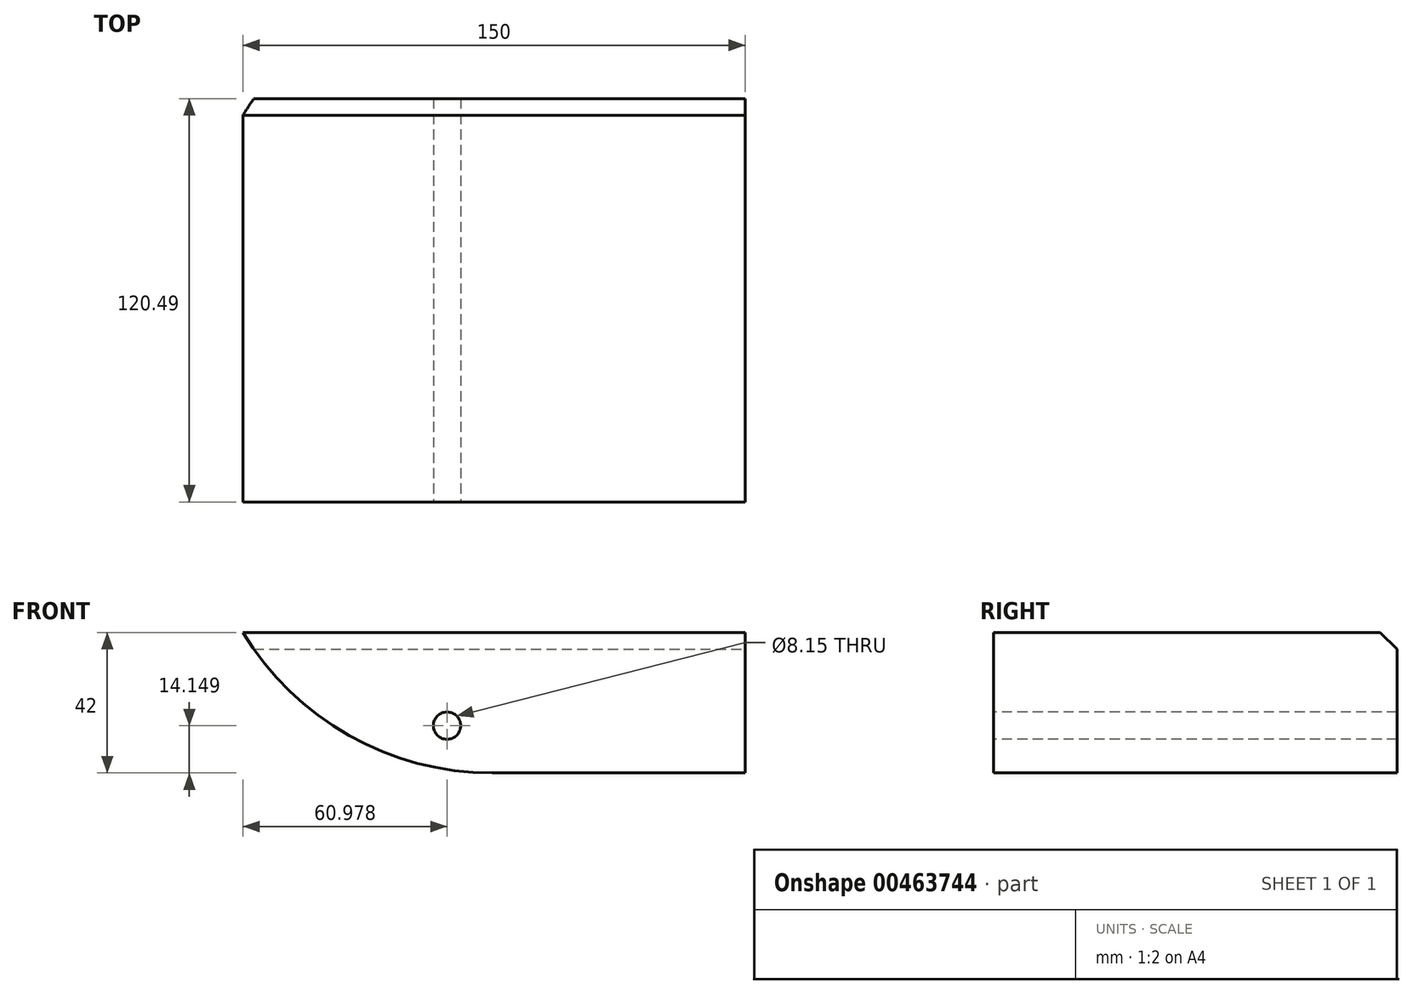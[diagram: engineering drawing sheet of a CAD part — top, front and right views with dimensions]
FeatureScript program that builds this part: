
annotation { "Feature Type Name" : "Feature", "Feature Type Description" : "" }
export const myFeature = defineFeature(function(context is Context, id is Id, definition is map)
    precondition{}
    {
        {
            var Q0;
            Q0=qCreatedBy(makeId("Top.planeOp"),FACE);
            var sketch = newSketch(context, id + "F0", { "sketchPlane" : qUnion([Q0])});
            skLineSegment(sketch, "E0.bottom", {"start": v(-96.86, 0) * mm, "end": v(53.14, 0) * mm});
            skLineSegment(sketch, "E0.top", {"start": v(-96.86, -120.49) * mm, "end": v(53.14, -120.49) * mm});
            skLineSegment(sketch, "E0.left", {"start": v(-96.86, 0) * mm, "end": v(-96.86, -120.49) * mm});
            skLineSegment(sketch, "E0.right", {"start": v(53.14, 0) * mm, "end": v(53.14, -120.49) * mm});
            skSolve(sketch);
        }
        {
            var Q0;
            Q0 = qSketchRegion(id + "F0", true);
            extrude(context, id + "F1", {"entities" : qUnion([Q0]), "depth" : 42 * mm});
        }
        {
            var Q0;
            Q0=makeQuery(id+"F1.opExtrude","CAP_EDGE",EDGE,{"disambiguationData":[OSD([sQuery(id+"F0.wireOp",EDGE,"E0.bottom")])],"isStart":false});
            chamfer(context, id + "F2", {"entities" : qUnion([Q0]), "width" : 5 * mm, "tangentPropagation" : true});
        }
        {
            var Q0;
            Q0=makeQuery(id+"F1.opExtrude","CAP_EDGE",EDGE,{"disambiguationData":[OSD([sQuery(id+"F0.wireOp",EDGE,"E0.left")])],"isStart":true});
            fillet(context, id + "F3", {"entities" : qUnion([Q0]), "radius" : 86.9 * mm, "tangentPropagation" : true, "allowEdgeOverflow" : false});
        }
        {
            var Q0;
            Q0=makeQuery(id+"F1.opExtrude","CAP_FACE",FACE,{"disambiguationData":[OSD([sQuery(id+"F0.wireOp",EDGE,"E0.bottom"),sQuery(id+"F0.wireOp",EDGE,"E0.top"),sQuery(id+"F0.wireOp",EDGE,"E0.left"),sQuery(id+"F0.wireOp",EDGE,"E0.right")])],"isStart":true});
            var sketch = newSketch(context, id + "F4", { "sketchPlane" : qUnion([Q0])});
            skCircle(sketch, "E1", {"center": v(11.86, 61.11) * mm, "radius": 25.8 * mm});
            skSolve(sketch);
        }
        {
            var Q0;
            Q0=sQuery(id+"F4.wireOp",EDGE,"E1");
            extrude(context, id + "F5", {"bodyType" : ToolBodyType.SURFACE, "surfaceEntities" : qUnion([Q0]), "depth" : 120 * mm});
        }
        {
            var Q0;
            Q0=makeQuery(id+"F1.opExtrude","SWEPT_FACE",FACE,{"disambiguationData":[OSD([sQuery(id+"F0.wireOp",EDGE,"E0.top")])]});
            var sketch = newSketch(context, id + "F6", { "sketchPlane" : qUnion([Q0])});
            skCircle(sketch, "E2", {"center": v(-35.88, 14.15) * mm, "radius": 4.07 * mm});
            skSolve(sketch);
        }
        {
            var Q0;
            Q0=makeQuery(id+"F6.imprint","IMPRINT",FACE,{"disambiguationData":[TD([[makeQuery(id+"F6.imprint","IMPRINT",EDGE,{"derivedFrom":sQuery(id+"F6.wireOp",EDGE,"E2")}),1.0]])]});
            extrude(context, id + "F7", {"entities" : qUnion([Q0]), "operationType" : NewBodyOperationType.REMOVE, "oppositeDirection" : true, "depth" : 192 * mm});
        }
    });
